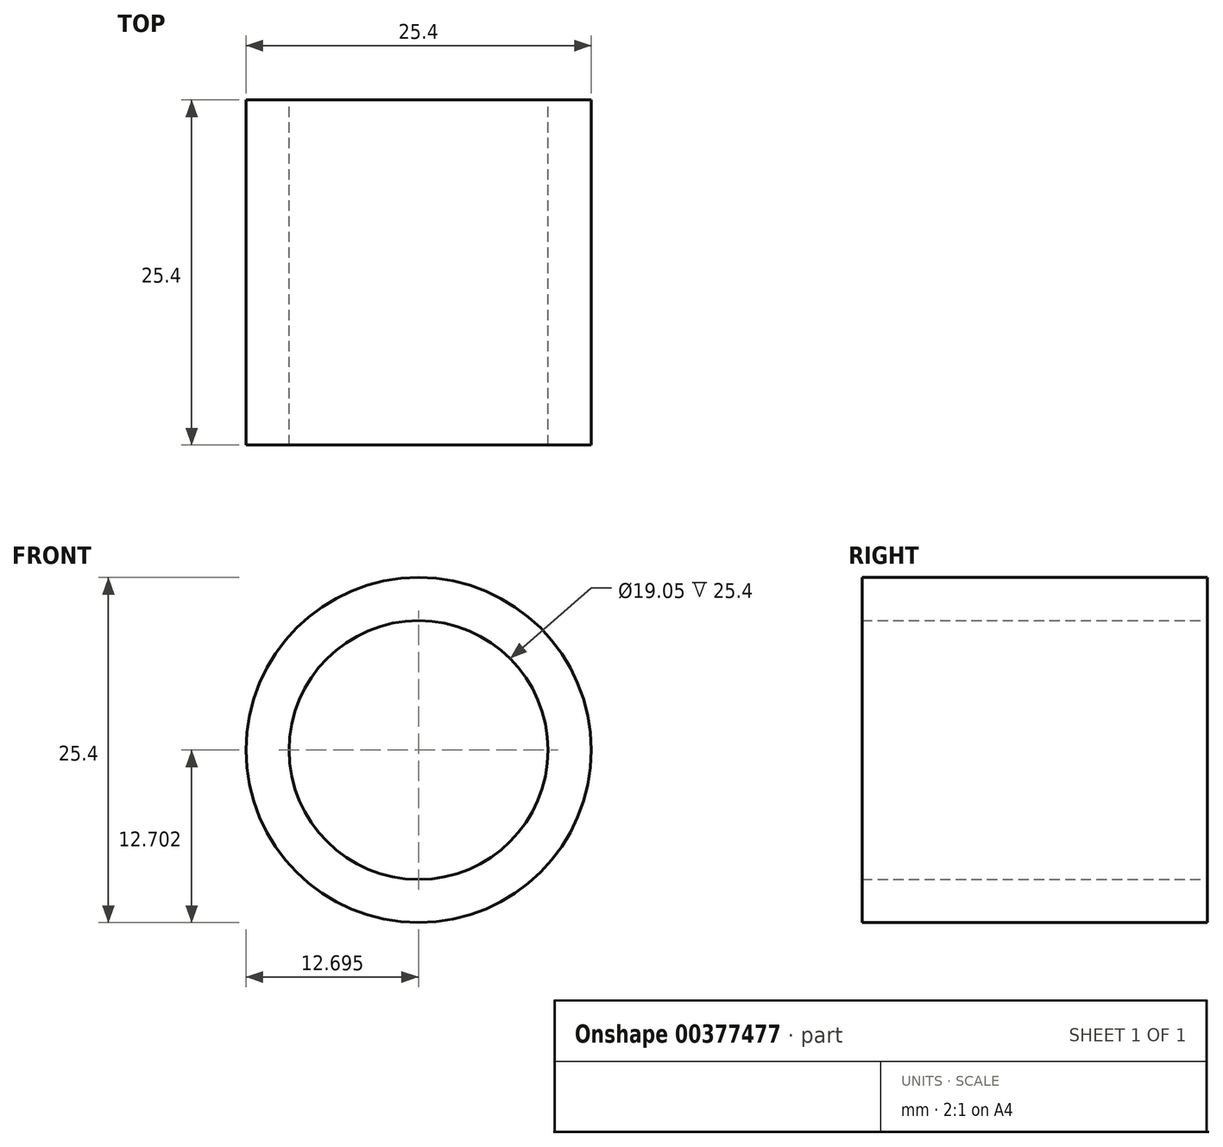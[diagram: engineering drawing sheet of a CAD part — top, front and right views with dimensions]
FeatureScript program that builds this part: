
annotation { "Feature Type Name" : "Feature", "Feature Type Description" : "" }
export const myFeature = defineFeature(function(context is Context, id is Id, definition is map)
    precondition{}
    {
        {
            var Q0;
            Q0=qCreatedBy(makeId("Front.planeOp"),FACE);
            var sketch = newSketch(context, id + "F0", { "sketchPlane" : qUnion([Q0])});
            skCircle(sketch, "E0", {"center": v(-132.85, 36.11) * mm, "radius": 9.53 * mm});
            skCircle(sketch, "E1", {"center": v(-132.85, 36.11) * mm, "radius": 12.7 * mm});
            skSolve(sketch);
        }
        {
            var Q0;
            Q0=makeQuery(id+"F0.imprint","IMPRINT",FACE,{"disambiguationData":[TD([[makeQuery(id+"F0.imprint","IMPRINT",EDGE,{"derivedFrom":sQuery(id+"F0.wireOp",EDGE,"E0")}),-1.0]])]});
            extrude(context, id + "F1", {"entities" : qUnion([Q0]), "depth" : 25.4 * mm});
        }
    });
